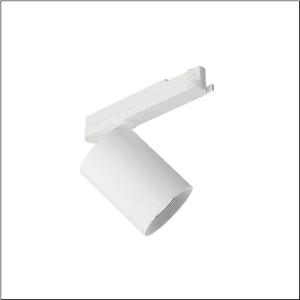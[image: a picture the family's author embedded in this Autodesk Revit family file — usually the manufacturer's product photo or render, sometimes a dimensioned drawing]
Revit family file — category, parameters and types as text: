
# Revit family: spot_21_51se14mba5b
name_source: partatom
category: Lighting Fixtures
units: mm (PartAtom-declared; Revit-internal decimal feet)

## family parameters
Cut with Voids When Loaded = No
Host = Face
Light Source = No
Part Type = Normal
Room Calculation Point = No
Round Connector Dimension = Use Diameter
Shared = No

## types (1)
- --- (1 x LED, 5340 lm, 41.8 W, 2700K)
    Apparent Load = 42 VA
    CIE Flux Codes = 96 99 100 100 100
    Color Rendering = 90
    Color Temperature = 2700K
    Default Elevation = 1800 mm
    Description = Spot 21, directional spotlight, light control with lens, of PMMA, LED rated luminous flux: 5.030lm, light colour: 927, control gear: ECG Multilumen, with 3-phase adapter, mains connection: 220..240V, AC, 50/60Hz, of aluminium, traffic white (RAL 9016), length: 213mm, diameter: 105mm, protection rating (complete): IP20, insulation class (complete): insulation class I (protective earthing), certification: CE, impact resistance: IK02, permissible ambient temperature for indoor applications: -20..+40°C, packaging unit: 1 piece
    Height = 175 mm
    Lamp = 1 x LED
    Lamp Light Flux = 5340 lm
    Lamp Power = 41.8 W
    Lamp count = 1
    Length = 105 mm
    Luminous efficacy = 128 lm/W
    Manufacturer = Siteco
    ModVariant = No
    Model = 51SE14MBA5B
    Mounting Place = Ceiling
    Mounting Type = Pendant
    Number of Poles = 1
    OnlyDefault = Yes
    Power Factor = 1
    Product Name = Spot 21
    Product group = directional spotlight
    ProductGroupID = 905
    Protection Class = Protection class I
    Protection Degree = IP 20
    RLX_Detail_Level = 1
    RLX_Emergency_Light_Flux = 0 lm
    RLX_Emergency_Type = 0
    RLX_Emergency_Type_DB = No
    RlxData = <blob elided: 17617 chars, md5=04f53426>
    Socket = socket
    Standby Power = 0 W
    System Light Flux = 5340 lm
    System Power = 42 W
    Type Comments = factory setting: luminous flux: 100 % | (ON | ON | ON | ON) | 1050 mA
    Type Image = l_1003976.jpg
    URL = http://relux.com
    VarID = @adj_074997
    Voltage = 0 V
    Weight = 0.00 kg
    Width = 0 mm  [stored 0 ft]

note: [stored X ft] marks values corroborated as IEEE doubles in the binary element streams (Revit-internal decimal feet)

## geometry (parser evidence)
native form markers: Blend x4, Sweep x10
no freeform markers — native parametric forms only
